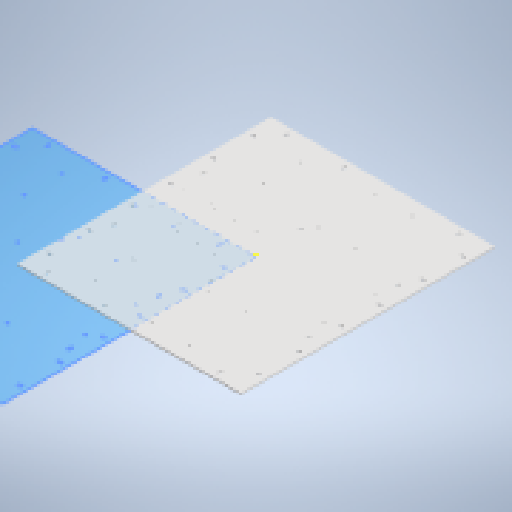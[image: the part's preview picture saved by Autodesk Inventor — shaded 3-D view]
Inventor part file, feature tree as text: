
AUTODESK INVENTOR PART (.ipt)
format: ipt  version: 2024 (Build 280153000, 153)  size: 393,728 bytes
history: native  units: mm
features: sketch x5, extrude x3, other x1
ambient origin geometry x8: Origin, YZ Plane, XZ Plane, XY Plane, X Axis, Y Axis, Z Axis, Center Point
bodies: Body1 (feature_tree)
feature tree (9):
  other  "솔리드1"
  extrude  "돌출1"  Depth=390.0mm
  sketch  "스케치4"
  extrude  "돌출3"  Depth=442.0mm
  sketch  "스케치7"
  extrude  "돌출4"  Depth=3.0mm TaperAngle=0.0deg
  sketch  "스케치1"
  sketch  "스케치6"
  sketch  "스케치8"
